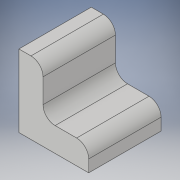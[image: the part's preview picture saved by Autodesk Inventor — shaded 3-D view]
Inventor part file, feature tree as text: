
AUTODESK INVENTOR PART (.ipt)
format: ipt  version: 2018 (Build 220112000, 112)  size: 105,984 bytes
history: native  units: in
note: dims shown in document units (in); Inventor stores cm internally (conversion verified against a paired STEP export)
features: extrude x1, fillet x1, sketch x1
ambient origin geometry x8: Origin, YZ Plane, XZ Plane, XY Plane, X Axis, Y Axis, Z Axis, Center Point
bodies: Solid1 (feature_tree)
feature tree (3):
  extrude  "Extrusion1"  Depth=0.5in
  fillet  "Fillet1"  Radius=1.0in
  sketch  "Sketch1"  dims[d0=1.5in d1=0.5in d2=1.0in d3=1.5in d4=0.0in d5=0.25in]
